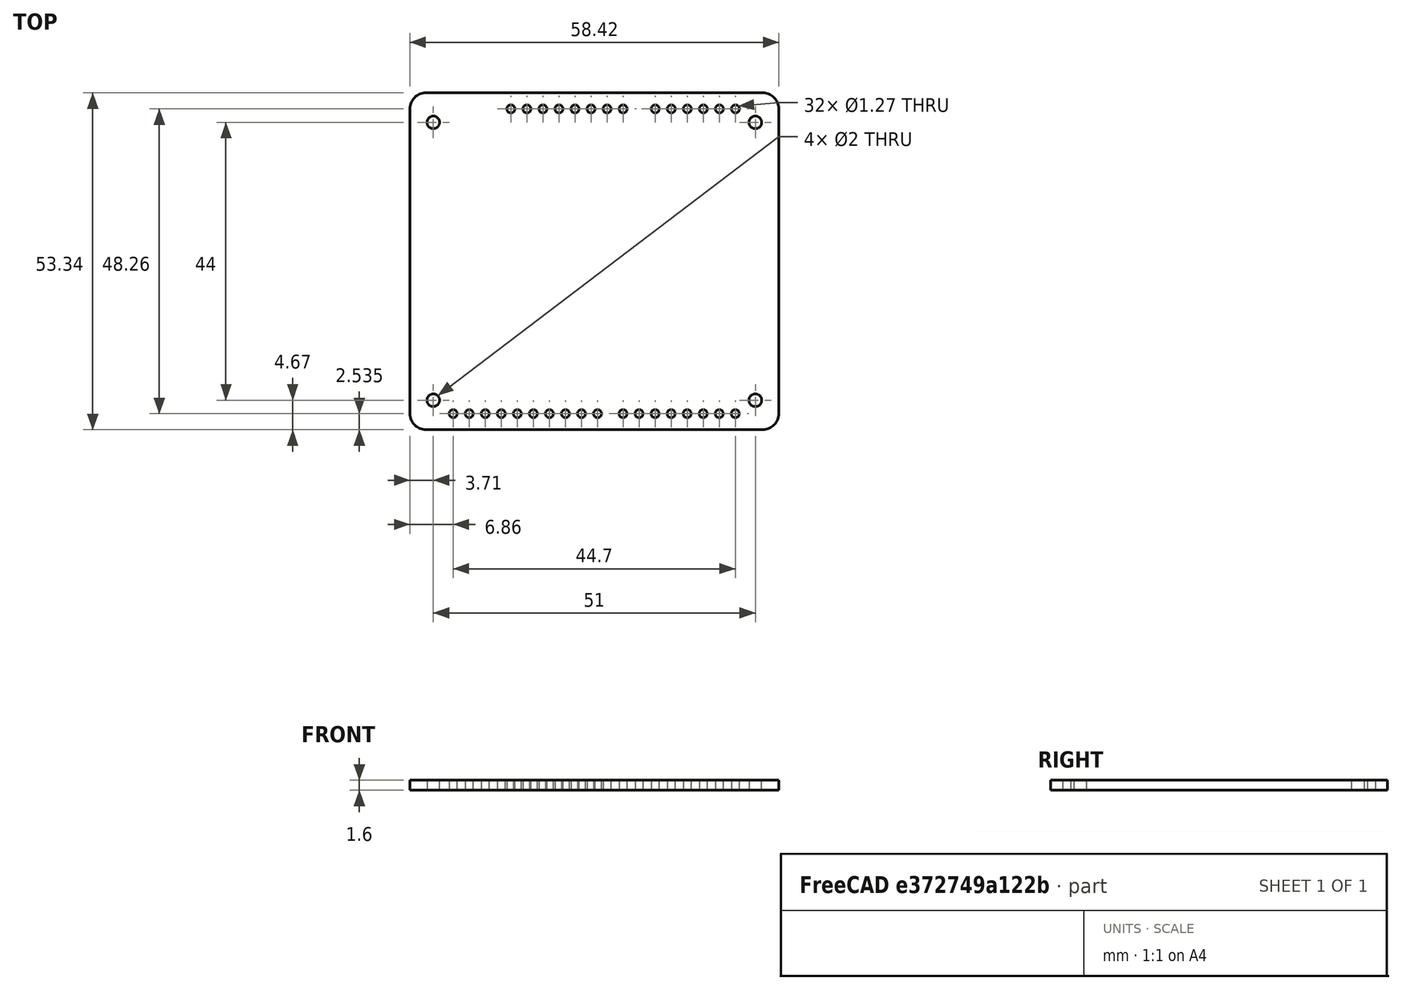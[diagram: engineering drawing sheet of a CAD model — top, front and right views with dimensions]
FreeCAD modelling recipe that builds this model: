
FCSTD DOCUMENT  (FreeCAD 0.14R3702 (Git))
Label: kitt-mb01
License: CC-BY 3.0
LicenseURL: http://creativecommons.org/licenses/by/3.0/
objects: Sketcher::SketchObject×9, Part::Extrusion×9, Part::Feature×5, Part::MultiFuse×2, Part::Cut×2, Part::Compound×2
note: 29 computed .brp shape members not serialized (recipe doc carries the construction recipe); baked Part::Feature solids carry a one-line shape summary decoded from their .brp

FEATURE [Sketcher::SketchObject] Sketch
  Placement = pos=(1.17,4.67,0) rot=(0,0,1;0rad)
  sketch-geometry (1):
    g0: Circle CenterX=0 CenterY=0 CenterZ=0 NormalX=0 NormalY=0 NormalZ=1 Radius=1
FEATURE [Sketcher::SketchObject] Sketch001
  Placement = pos=(52.17,4.67,0) rot=(0,0,1;0rad)
  sketch-geometry (1):
    g0: Circle CenterX=0 CenterY=0 CenterZ=0 NormalX=0 NormalY=0 NormalZ=1 Radius=1
FEATURE [Sketcher::SketchObject] Sketch002
  Placement = pos=(1.17,48.67,0) rot=(0,0,1;0rad)
  sketch-geometry (1):
    g0: Circle CenterX=0 CenterY=0 CenterZ=0 NormalX=0 NormalY=0 NormalZ=1 Radius=1
FEATURE [Sketcher::SketchObject] Sketch003
  Placement = pos=(52.17,48.67,0) rot=(0,0,1;0rad)
  sketch-geometry (1):
    g0: Circle CenterX=0 CenterY=0 CenterZ=0 NormalX=0 NormalY=0 NormalZ=1 Radius=1
FEATURE [Sketcher::SketchObject] Sketch004
  sketch-geometry (8):
    g0: LineSegment StartX=0 StartY=53.34 StartZ=0 EndX=53.34 EndY=53.34 EndZ=0
    g1: LineSegment StartX=0 StartY=0 StartZ=0 EndX=53.34 EndY=0 EndZ=0
    g2: ArcOfCircle CenterX=0 CenterY=2.54 CenterZ=0 NormalX=0 NormalY=0 NormalZ=1 Radius=2.54 StartAngle=3.14159 EndAngle=4.71239
    g3: ArcOfCircle CenterX=0 CenterY=50.8 CenterZ=0 NormalX=0 NormalY=0 NormalZ=1 Radius=2.54 StartAngle=1.5708 EndAngle=3.14159
    g4: LineSegment StartX=-2.54 StartY=50.8 StartZ=0 EndX=-2.54 EndY=2.54 EndZ=0
    g5: ArcOfCircle CenterX=53.34 CenterY=50.8 CenterZ=0 NormalX=0 NormalY=0 NormalZ=1 Radius=2.54 StartAngle=0 EndAngle=1.5708
    g6: LineSegment StartX=55.88 StartY=50.8 StartZ=0 EndX=55.88 EndY=2.54 EndZ=0
    g7: ArcOfCircle CenterX=53.34 CenterY=2.54 CenterZ=0 NormalX=0 NormalY=0 NormalZ=1 Radius=2.54 StartAngle=4.71239 EndAngle=6.28319
  constraints (9):
    c: Coincident(g1,g-1)
    c: Coincident(g2,g-1)
    c: Coincident(g4,g3)
    c: Coincident(g4,g2)
    c: Coincident(g5,g0)
    c: Coincident(g6,g5)
    c: Coincident(g7,g1)
    c: Coincident(g7,g6)
    c: Coincident(g0,g3)
FEATURE [Sketcher::SketchObject] Sketch006
  Placement = pos=(0.75,0.63,13) rot=(0,0,1;0rad)
  sketch-geometry (8):
    g0: Circle CenterX=12.7 CenterY=50.165 CenterZ=0 NormalX=0 NormalY=0 NormalZ=1 Radius=0.635
    g1: Circle CenterX=15.24 CenterY=50.165 CenterZ=0 NormalX=0 NormalY=0 NormalZ=1 Radius=0.635
    g2: Circle CenterX=17.78 CenterY=50.165 CenterZ=0 NormalX=0 NormalY=0 NormalZ=1 Radius=0.635
    g3: Circle CenterX=20.32 CenterY=50.165 CenterZ=0 NormalX=0 NormalY=0 NormalZ=1 Radius=0.635
    g4: Circle CenterX=22.86 CenterY=50.165 CenterZ=0 NormalX=0 NormalY=0 NormalZ=1 Radius=0.635
    g5: Circle CenterX=25.4 CenterY=50.165 CenterZ=0 NormalX=0 NormalY=0 NormalZ=1 Radius=0.635
    g6: Circle CenterX=27.94 CenterY=50.165 CenterZ=0 NormalX=0 NormalY=0 NormalZ=1 Radius=0.635
    g7: Circle CenterX=30.48 CenterY=50.165 CenterZ=0 NormalX=0 NormalY=0 NormalZ=1 Radius=0.635
FEATURE [Part::Feature] arduino_uno
  Placement = pos=(-14.478,53.34,9) rot=(0.57735,0.57735,-0.57735;4.18879rad)
  shape: bbox 68.58 x 53.34 x 1.65 mm, 174 faces, 0 solids (baked)
FEATURE [Part::Feature] arduino_uno001
  Placement = pos=(49.03,50.77,0) rot=(0,0.707107,0.707107;3.14159rad)
  shape: bbox 15.24 x 2.41 x 10.55 mm, 210 faces, 0 solids (baked)
FEATURE [Part::Feature] arduino_uno002
  Placement = pos=(49,2.54,0) rot=(0,0.707107,0.707107;3.14159rad)
  shape: bbox 20.32 x 2.41 x 10.55 mm, 278 faces, 0 solids (baked)
FEATURE [Part::Feature] arduino_uno003
  Placement = pos=(31.23,50.77,0) rot=(0,0.707107,0.707107;3.14159rad)
  shape: bbox 20.32 x 2.41 x 10.55 mm, 278 faces, 0 solids (baked)
FEATURE [Part::Feature] arduino_uno004
  Placement = pos=(27.204,2.535,0) rot=(0,0.707107,0.707107;3.14159rad)
  shape: bbox 25.4 x 2.41 x 10.55 mm, 346 faces, 0 solids (baked)
FEATURE [Sketcher::SketchObject] Sketch007
  Placement = pos=(-3.3,-47.63,13) rot=(0,0,1;0rad)
  sketch-geometry (10):
    g0: Circle CenterX=10.16 CenterY=50.165 CenterZ=0 NormalX=0 NormalY=0 NormalZ=1 Radius=0.635
    g1: Circle CenterX=7.62 CenterY=50.165 CenterZ=0 NormalX=0 NormalY=0 NormalZ=1 Radius=0.635
    g2: Circle CenterX=12.7 CenterY=50.165 CenterZ=0 NormalX=0 NormalY=0 NormalZ=1 Radius=0.635
    g3: Circle CenterX=15.24 CenterY=50.165 CenterZ=0 NormalX=0 NormalY=0 NormalZ=1 Radius=0.635
    g4: Circle CenterX=17.78 CenterY=50.165 CenterZ=0 NormalX=0 NormalY=0 NormalZ=1 Radius=0.635
    g5: Circle CenterX=20.32 CenterY=50.165 CenterZ=0 NormalX=0 NormalY=0 NormalZ=1 Radius=0.635
    g6: Circle CenterX=22.86 CenterY=50.165 CenterZ=0 NormalX=0 NormalY=0 NormalZ=1 Radius=0.635
    g7: Circle CenterX=25.4 CenterY=50.165 CenterZ=0 NormalX=0 NormalY=0 NormalZ=1 Radius=0.635
    g8: Circle CenterX=27.94 CenterY=50.165 CenterZ=0 NormalX=0 NormalY=0 NormalZ=1 Radius=0.635
    g9: Circle CenterX=30.48 CenterY=50.165 CenterZ=0 NormalX=0 NormalY=0 NormalZ=1 Radius=0.635
FEATURE [Sketcher::SketchObject] Sketch008
  Placement = pos=(23.6,-47.63,13) rot=(0,0,1;0rad)
  sketch-geometry (8):
    g0: Circle CenterX=10.16 CenterY=50.165 CenterZ=0 NormalX=0 NormalY=0 NormalZ=1 Radius=0.635
    g1: Circle CenterX=7.62 CenterY=50.165 CenterZ=0 NormalX=0 NormalY=0 NormalZ=1 Radius=0.635
    g2: Circle CenterX=12.7 CenterY=50.165 CenterZ=0 NormalX=0 NormalY=0 NormalZ=1 Radius=0.635
    g3: Circle CenterX=15.24 CenterY=50.165 CenterZ=0 NormalX=0 NormalY=0 NormalZ=1 Radius=0.635
    g4: Circle CenterX=17.78 CenterY=50.165 CenterZ=0 NormalX=0 NormalY=0 NormalZ=1 Radius=0.635
    g5: Circle CenterX=20.32 CenterY=50.165 CenterZ=0 NormalX=0 NormalY=0 NormalZ=1 Radius=0.635
    g6: Circle CenterX=22.86 CenterY=50.165 CenterZ=0 NormalX=0 NormalY=0 NormalZ=1 Radius=0.635
    g7: Circle CenterX=25.4 CenterY=50.165 CenterZ=0 NormalX=0 NormalY=0 NormalZ=1 Radius=0.635
FEATURE [Sketcher::SketchObject] Sketch009
  Placement = pos=(23.62,0.63,13) rot=(0,0,1;0rad)
  sketch-geometry (6):
    g0: Circle CenterX=12.7 CenterY=50.165 CenterZ=0 NormalX=0 NormalY=0 NormalZ=1 Radius=0.635
    g1: Circle CenterX=15.24 CenterY=50.165 CenterZ=0 NormalX=0 NormalY=0 NormalZ=1 Radius=0.635
    g2: Circle CenterX=17.78 CenterY=50.165 CenterZ=0 NormalX=0 NormalY=0 NormalZ=1 Radius=0.635
    g3: Circle CenterX=20.32 CenterY=50.165 CenterZ=0 NormalX=0 NormalY=0 NormalZ=1 Radius=0.635
    g4: Circle CenterX=22.86 CenterY=50.165 CenterZ=0 NormalX=0 NormalY=0 NormalZ=1 Radius=0.635
    g5: Circle CenterX=25.4 CenterY=50.165 CenterZ=0 NormalX=0 NormalY=0 NormalZ=1 Radius=0.635
FEATURE [Part::Extrusion] Extrude
  Base = -> Sketch004
  Dir = (0,0,1.6)
  Solid = true
FEATURE [Part::Extrusion] Extrude001
  Base = -> Sketch007
  Dir = (0,0,2)
  Solid = true
FEATURE [Part::Extrusion] Extrude002
  Base = -> Sketch009
  Dir = (0,0,2)
  Solid = true
FEATURE [Part::Extrusion] Extrude003
  Base = -> Sketch008
  Dir = (0,0,2)
  Solid = true
FEATURE [Part::Extrusion] Extrude004
  Base = -> Sketch006
  Dir = (0,0,2)
  Solid = true
FEATURE [Part::MultiFuse] Fusion
  Placement = pos=(0,0,-13) rot=(0,0,1;0rad)
  Shapes = -> [Extrude004,Extrude003,Extrude001,Extrude002]
FEATURE [Part::Cut] Cut
  Base = -> Extrude
  Tool = -> Fusion
FEATURE [Part::Extrusion] Extrude005
  Base = -> Sketch001
  Dir = (0,0,2)
  Solid = true
FEATURE [Part::Extrusion] Extrude006
  Base = -> Sketch003
  Dir = (0,0,2)
  Solid = true
FEATURE [Part::Extrusion] Extrude007
  Base = -> Sketch002
  Dir = (0,0,2)
  Solid = true
FEATURE [Part::Extrusion] Extrude008
  Base = -> Sketch
  Dir = (0,0,2)
  Solid = true
FEATURE [Part::MultiFuse] Fusion001
  Shapes = -> [Extrude005,Extrude007,Extrude006,Extrude008]
FEATURE [Part::Cut] Cut001  label="kitt-mb01.pcb"
  Base = -> Cut
  Tool = -> Fusion001
FEATURE [Part::Compound] Compound  label="kitt-mb01.socket"
  Links = -> [arduino_uno004,arduino_uno003,arduino_uno002,arduino_uno001]
  Placement = pos=(0,0,1.6) rot=(0,0,1;0rad)
FEATURE [Part::Compound] Compound001  label="kitt-mb01"
  Links = -> [Cut001,Compound]
